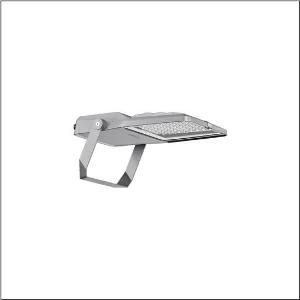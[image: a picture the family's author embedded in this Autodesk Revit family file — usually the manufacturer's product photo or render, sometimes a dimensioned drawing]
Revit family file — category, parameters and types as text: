
# Revit family: floodlight_fl_21_iq_mini___pl61_5xa7771c2c1a_d716
name_source: partatom
category: Lighting Fixtures
units: mm (PartAtom-declared; Revit-internal decimal feet)

## family parameters
Cut with Voids When Loaded = No
Host = Face
Light Source = No
Part Type = Normal
Room Calculation Point = No
Round Connector Dimension = Use Diameter
Shared = No

## types (1)
- --- (1 x LED, 11980 lm, 87.2 W, 3000K)
    Apparent Load = 87 VA
    CIE Flux Codes = 33 65 98 100 100
    Color Rendering = 70
    Color Temperature = 3000K
    Default Elevation = 1800 mm
    Description = Floodlight FL 21 iQ mini, floodlight, primary light control with lens, of PMMA, primary optical cover: protective disc, of toughened safety glass, transparent, light distribution: PL61, light emission: direct distribution, installation type: surface-mounted, lamps: LED, High Power LED, rated values: 11.980lm | 87,2W | 137,4lm/W (begin service life); end service life: 11.980lm | 92,1W; at 50% lumin. flux: 5.990lm | 40,1W | 149,4lm/W, colour temperature: 3000K, colour rendering: CRI > 70, light colour: 730, light setting 1 begin service life: 100% | 11.980lm | 87,2W | 137,4lm/W | 3.000K, light setting 1 end service life: 92,1W, further light settings possible, control: Auto-Match, Temp-Guard, Lumen-Switch, Night-Set, Smart-Wire, Light-Fading, Desk-Remote (wireless, voltage-free reading and setting of iQ features in the workshop via application-optimized NFC function/RFID function), optimised constant luminous flux control (CLO 2.0), pre-setting: linear dimming characteristic, with terminal, 6-pole, mains connection: 220..240V, AC, 50/60Hz, luminaire housing, of diecast aluminium, powder-coated, SITECO metallic grey (DB 702S), corrosivity category C5 mid according to DIN EN ISO 12944suitable for swimming poolschlorine-resistant, sealing non-destructively replaceable, mounting bracket, of steel, galvanised, powder-coated, SITECO metallic grey (DB 702S), protection rating (complete): IP66, insulation class (complete): insulation class II (safety insulation), certification: CE, ENEC, VDE, protection symbol: D, impact resistance: IK08, permissible operating ambient temperature: -40..+40°C, permissible operating ambient temperature for outdoor applications: -40..+50°C, standard: DIN EN 12944, LABS conformity tested according to VDMA 24364:2018-05, packaging unit: 1 piece

Light Distribution: PL61
    Height = 70 mm
    Lamp = 1 x LED
    Lamp Light Flux = 11980 lm
    Lamp Power = 87.2 W
    Lamp count = 1
    Length = 485 mm
    Luminous efficacy = 137 lm/W
    Manufacturer = Siteco
    ModVariant = No
    Model = 5XA7771C2C1A
    Mounting Place = Pole
    Mounting Type = Pole annexe
    Number of Poles = 1
    OnlyDefault = Yes
    Power Factor = 1
    Product Name = Floodlight FL 21 iQ mini | PL61
    Product group = floodlight | pylon annexe
    ProductGroupID = 6201
    Protection Class = Protection class II
    Protection Degree = IP 66
    RLX_Detail_Level = 1
    RLX_Emergency_Light_Flux = 0 lm
    RLX_Emergency_Type = 0
    RLX_Emergency_Type_DB = No
    RlxData = <blob elided: 96717 chars, md5=f62aef67>
    Socket = socket
    Standby Power = 0 W
    System Light Flux = 11980 lm
    System Power = 87 W
    Type Comments = factory setting: luminous flux: 100 % | dim-lin: 254 | 456 mA
    Type Image = l_1006845.jpg
    URL = http://relux.com
    VarID = @adj_174409
    Voltage = 0 V
    Weight = 0.00 kg
    Width = 337 mm

## geometry (parser evidence)
native form markers: Blend x4, Sweep x13
no freeform markers — native parametric forms only
